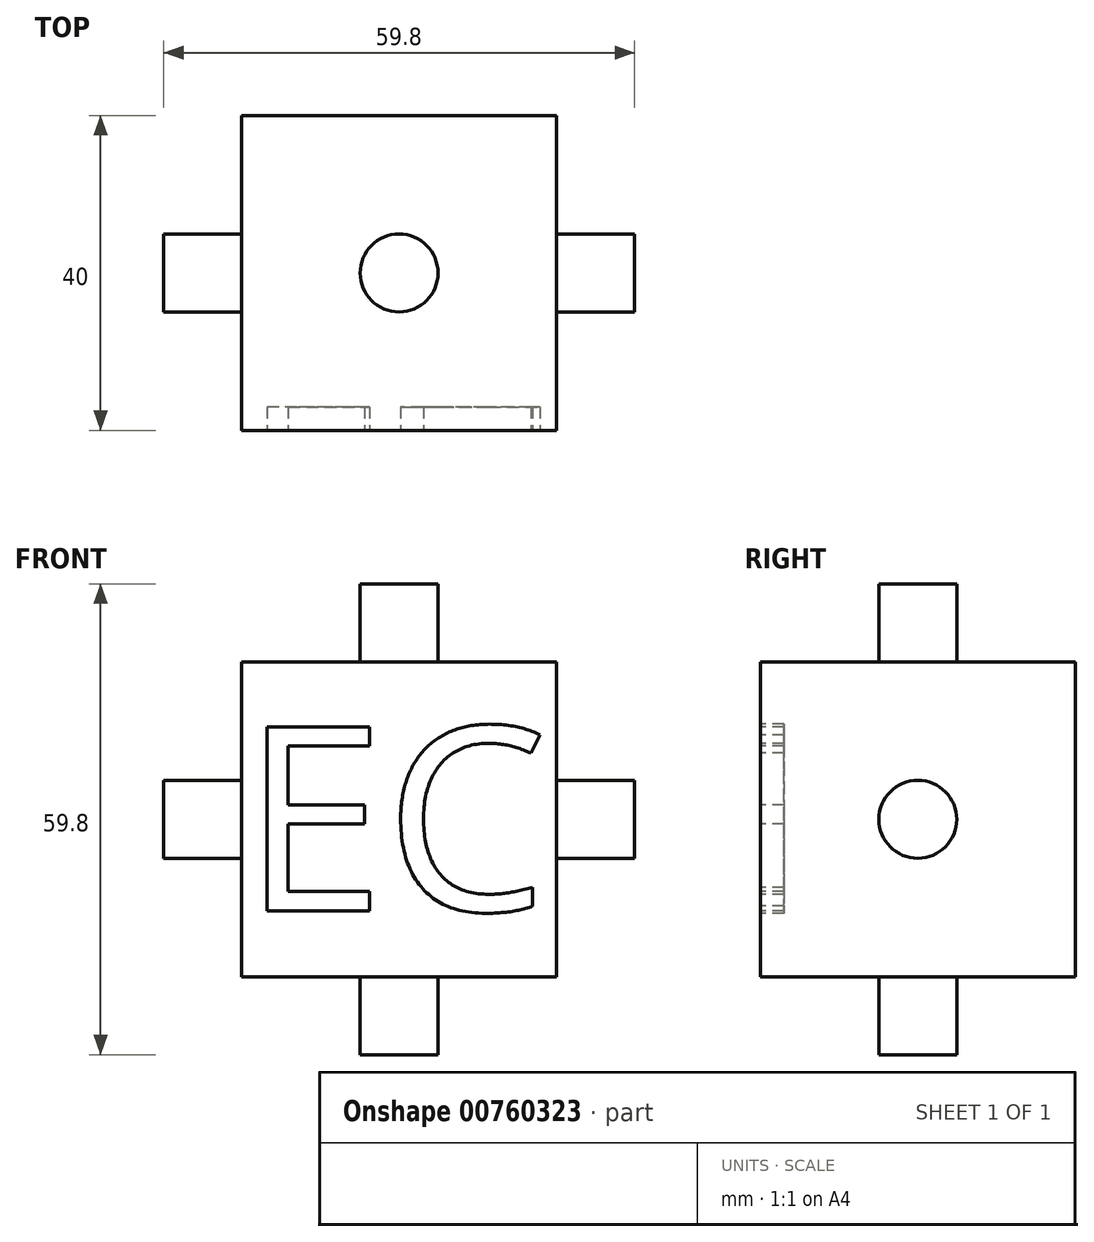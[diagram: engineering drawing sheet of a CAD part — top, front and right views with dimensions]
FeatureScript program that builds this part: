
annotation { "Feature Type Name" : "Feature", "Feature Type Description" : "" }
export const myFeature = defineFeature(function(context is Context, id is Id, definition is map)
    precondition{}
    {
        {
            var Q0;
            Q0=qCreatedBy(makeId("Front.planeOp"),FACE);
            var sketch = newSketch(context, id + "F0", { "sketchPlane" : qUnion([Q0])});
            skLineSegment(sketch, "E0", {"start": v(0, 0) * mm, "end": v(0, 40) * mm});
            skLineSegment(sketch, "E1", {"start": v(0, 40) * mm, "end": v(40, 40) * mm});
            skLineSegment(sketch, "E2", {"start": v(40, 40) * mm, "end": v(40, 0) * mm});
            skLineSegment(sketch, "E3", {"start": v(40, 0) * mm, "end": v(0, 0) * mm});
            skSolve(sketch);
        }
        {
            var Q0;
            Q0=makeQuery(id+"F0.imprint","IMPRINT",FACE,{"disambiguationData":[TD([[makeQuery(id+"F0.imprint","IMPRINT",EDGE,{"derivedFrom":sQuery(id+"F0.wireOp",EDGE,"E0")}),-1.0]])]});
            extrude(context, id + "F1", {"entities" : qUnion([Q0]), "depth" : 40 * mm, "offsetDistance" : 25 * mm});
        }
        {
            var Q0;
            Q0=makeQuery(id+"F1.opExtrude","CAP_FACE",FACE,{"disambiguationData":[OSD([sQuery(id+"F0.wireOp",EDGE,"E0"),sQuery(id+"F0.wireOp",EDGE,"E1"),sQuery(id+"F0.wireOp",EDGE,"E2"),sQuery(id+"F0.wireOp",EDGE,"E3")])],"isStart":false});
            var sketch = newSketch(context, id + "F2", { "sketchPlane" : qUnion([Q0])});
            skText(sketch, "E4", { "text": "EC", "fontName": "OpenSans-Regular.ttf"});
            const initialGuessF2  = {"E4": [0, 0.00838, 1, 0, 0.02357]};
            skSetInitialGuess(sketch, initialGuessF2);
            skSolve(sketch);
        }
        {
            var Q0;
            Q0 = qSketchRegion(id + "F2", true);
            extrude(context, id + "F3", {"entities" : qUnion([Q0]), "operationType" : NewBodyOperationType.REMOVE, "oppositeDirection" : true, "depth" : 3 * mm, "offsetDistance" : 25 * mm});
        }
        {
            var Q0;
            Q0=makeQuery(id+"F1.opExtrude","SWEPT_FACE",FACE,{"disambiguationData":[OSD([sQuery(id+"F0.wireOp",EDGE,"E1")])]});
            var sketch = newSketch(context, id + "F4", { "sketchPlane" : qUnion([Q0])});
            skCircle(sketch, "E5", {"center": v(20, -20) * mm, "radius": 4.95 * mm});
            skPoint(sketch, "E5.centerSnap0", {"position": v(0, -20) * mm});
            skPoint(sketch, "E5.centerSnap1", {"position": v(20, -40) * mm});
            skSolve(sketch);
        }
        {
            var Q0;
            Q0 = qSketchRegion(id + "F4", true);
            extrude(context, id + "F5", {"entities" : qUnion([Q0]), "operationType" : NewBodyOperationType.ADD, "depth" : 9.9 * mm, "offsetDistance" : 25 * mm});
        }
        {
            var Q0;
            Q0=makeQuery(id+"F1.opExtrude","SWEPT_FACE",FACE,{"disambiguationData":[OSD([sQuery(id+"F0.wireOp",EDGE,"E0")])]});
            var sketch = newSketch(context, id + "F6", { "sketchPlane" : qUnion([Q0])});
            skCircle(sketch, "E6", {"center": v(20, 20) * mm, "radius": 4.95 * mm});
            skPoint(sketch, "E6.centerSnap0", {"position": v(0, 20) * mm});
            skPoint(sketch, "E6.centerSnap1", {"position": v(20, 0) * mm});
            skSolve(sketch);
        }
        {
            var Q0;
            Q0 = qSketchRegion(id + "F6", true);
            extrude(context, id + "F7", {"entities" : qUnion([Q0]), "operationType" : NewBodyOperationType.ADD, "depth" : 9.9 * mm, "offsetDistance" : 25 * mm});
        }
        {
            var Q0;
            Q0=makeQuery(id+"F1.opExtrude","SWEPT_FACE",FACE,{"disambiguationData":[OSD([sQuery(id+"F0.wireOp",EDGE,"E2")])]});
            var sketch = newSketch(context, id + "F8", { "sketchPlane" : qUnion([Q0])});
            skCircle(sketch, "E7", {"center": v(-20, 20) * mm, "radius": 4.95 * mm});
            skPoint(sketch, "E7.centerSnap0", {"position": v(-40, 20) * mm});
            skPoint(sketch, "E7.centerSnap1", {"position": v(-20, 0) * mm});
            skSolve(sketch);
        }
        {
            var Q0;
            Q0 = qSketchRegion(id + "F8", true);
            extrude(context, id + "F9", {"entities" : qUnion([Q0]), "operationType" : NewBodyOperationType.ADD, "depth" : 9.9 * mm, "offsetDistance" : 25 * mm});
        }
        {
            var Q0;
            Q0=makeQuery(id+"F1.opExtrude","SWEPT_FACE",FACE,{"disambiguationData":[OSD([sQuery(id+"F0.wireOp",EDGE,"E3")])]});
            var sketch = newSketch(context, id + "F10", { "sketchPlane" : qUnion([Q0])});
            skCircle(sketch, "E8", {"center": v(20, 20) * mm, "radius": 4.95 * mm});
            skPoint(sketch, "E8.centerSnap0", {"position": v(0, 20) * mm});
            skPoint(sketch, "E8.centerSnap1", {"position": v(20, 0) * mm});
            skSolve(sketch);
        }
        {
            var Q0;
            Q0 = qSketchRegion(id + "F10", true);
            extrude(context, id + "F11", {"entities" : qUnion([Q0]), "operationType" : NewBodyOperationType.ADD, "depth" : 9.9 * mm, "offsetDistance" : 25 * mm});
        }
    });
